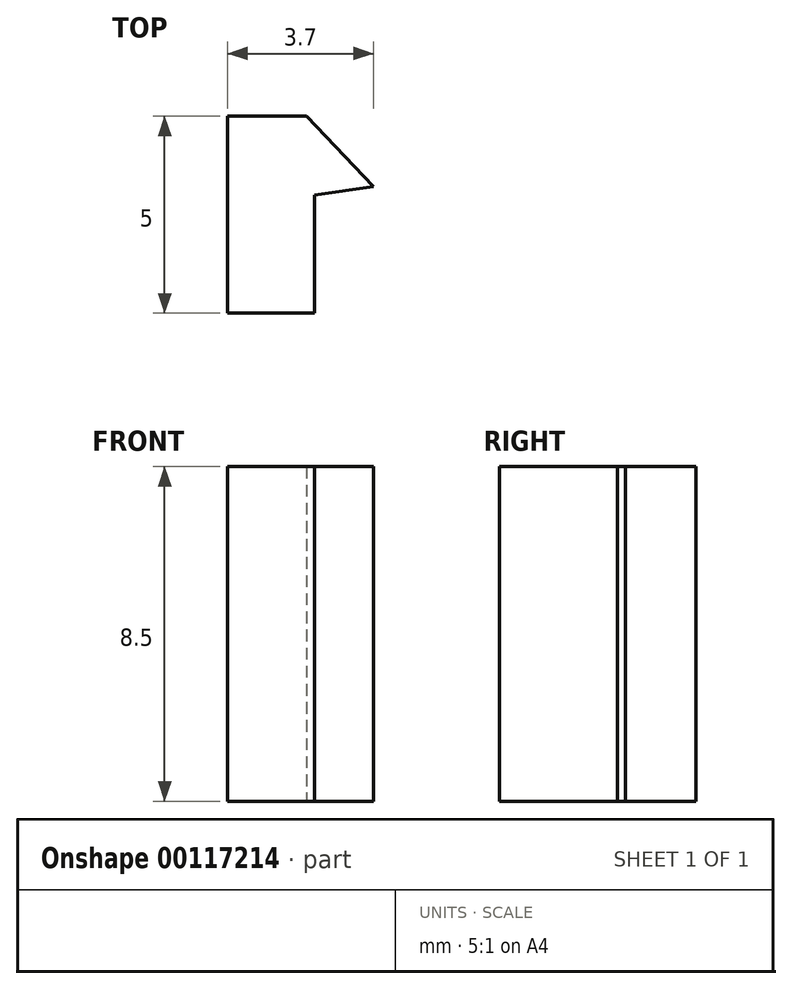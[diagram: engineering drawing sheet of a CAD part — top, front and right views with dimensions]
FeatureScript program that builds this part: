
annotation { "Feature Type Name" : "Feature", "Feature Type Description" : "" }
export const myFeature = defineFeature(function(context is Context, id is Id, definition is map)
    precondition{}
    {
        {
            var Q0;
            Q0=qCreatedBy(makeId("Top.planeOp"),FACE);
            var sketch = newSketch(context, id + "F0", { "sketchPlane" : qUnion([Q0])});
            skLineSegment(sketch, "E0", {"start": v(0, 0) * mm, "end": v(0, 5) * mm});
            skLineSegment(sketch, "E1", {"start": v(0, 5) * mm, "end": v(2, 5) * mm});
            skLineSegment(sketch, "E2", {"start": v(2, 5) * mm, "end": v(3.7, 3.21) * mm});
            skLineSegment(sketch, "E3", {"start": v(3.7, 3.21) * mm, "end": v(2.2, 3) * mm});
            skLineSegment(sketch, "E4", {"start": v(2.2, 3) * mm, "end": v(2.2, 0) * mm});
            skLineSegment(sketch, "E5", {"start": v(2.2, 0) * mm, "end": v(0, 0) * mm});
            skSolve(sketch);
        }
        {
            var Q0;
            Q0 = qSketchRegion(id + "F0", true);
            extrude(context, id + "F1", {"entities" : qUnion([Q0]), "depth" : 8.5 * mm});
        }
    });
